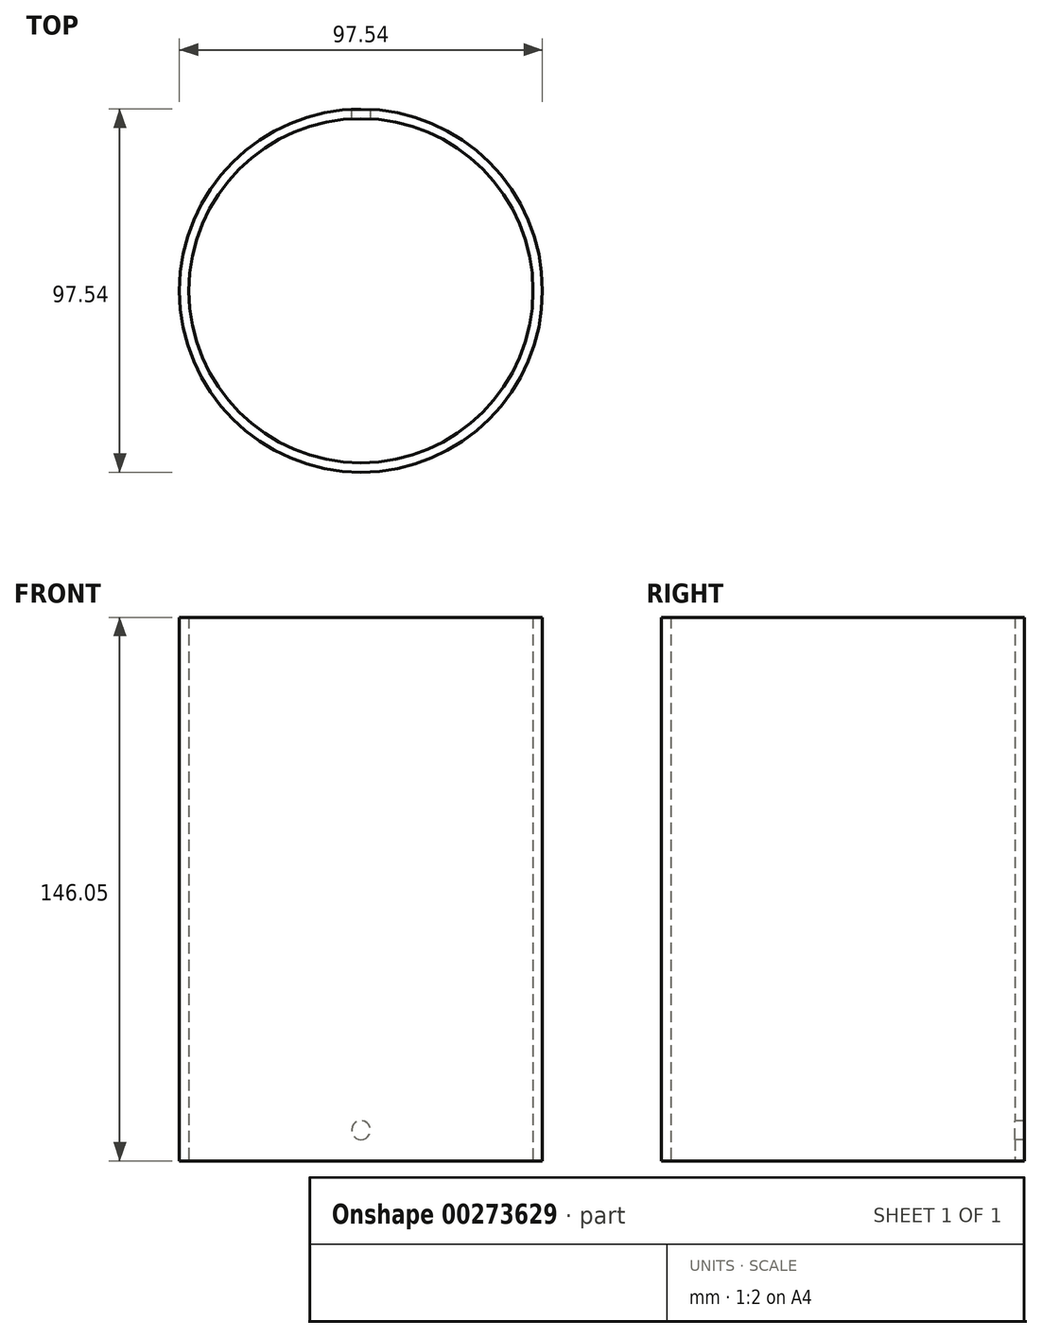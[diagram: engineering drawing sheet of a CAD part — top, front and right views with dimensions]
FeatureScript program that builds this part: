
annotation { "Feature Type Name" : "Feature", "Feature Type Description" : "" }
export const myFeature = defineFeature(function(context is Context, id is Id, definition is map)
    precondition{}
    {
        {
            var Q0;
            Q0=qCreatedBy(makeId("Top.planeOp"),FACE);
            var sketch = newSketch(context, id + "F0", { "sketchPlane" : qUnion([Q0])});
            skCircle(sketch, "E0", {"center": v(0, 0) * mm, "radius": 48.77 * mm});
            skCircle(sketch, "E1", {"center": v(0, 0) * mm, "radius": 46.23 * mm});
            skSolve(sketch);
        }
        {
            var Q0;
            Q0=makeQuery(id+"F0.imprint","IMPRINT",FACE,{"disambiguationData":[TD([[makeQuery(id+"F0.imprint","IMPRINT",EDGE,{"derivedFrom":sQuery(id+"F0.wireOp",EDGE,"E0")}),1.0]])]});
            extrude(context, id + "F1", {"entities" : qUnion([Q0]), "depth" : 146.05 * mm});
        }
        {
            var Q0;
            Q0=qCreatedBy(makeId("Front.planeOp"),FACE);
            var sketch = newSketch(context, id + "F2", { "sketchPlane" : qUnion([Q0])});
            skCircle(sketch, "E2", {"center": v(0, 8.26) * mm, "radius": 2.54 * mm});
            skSolve(sketch);
        }
        {
            var Q0;
            Q0 = qSketchRegion(id + "F2", true);
            extrude(context, id + "F3", {"entities" : qUnion([Q0]), "operationType" : NewBodyOperationType.REMOVE, "endBound" : BoundingType.THROUGH_ALL, "oppositeDirection" : true, "depth" : 25.4 * mm});
        }
    });
